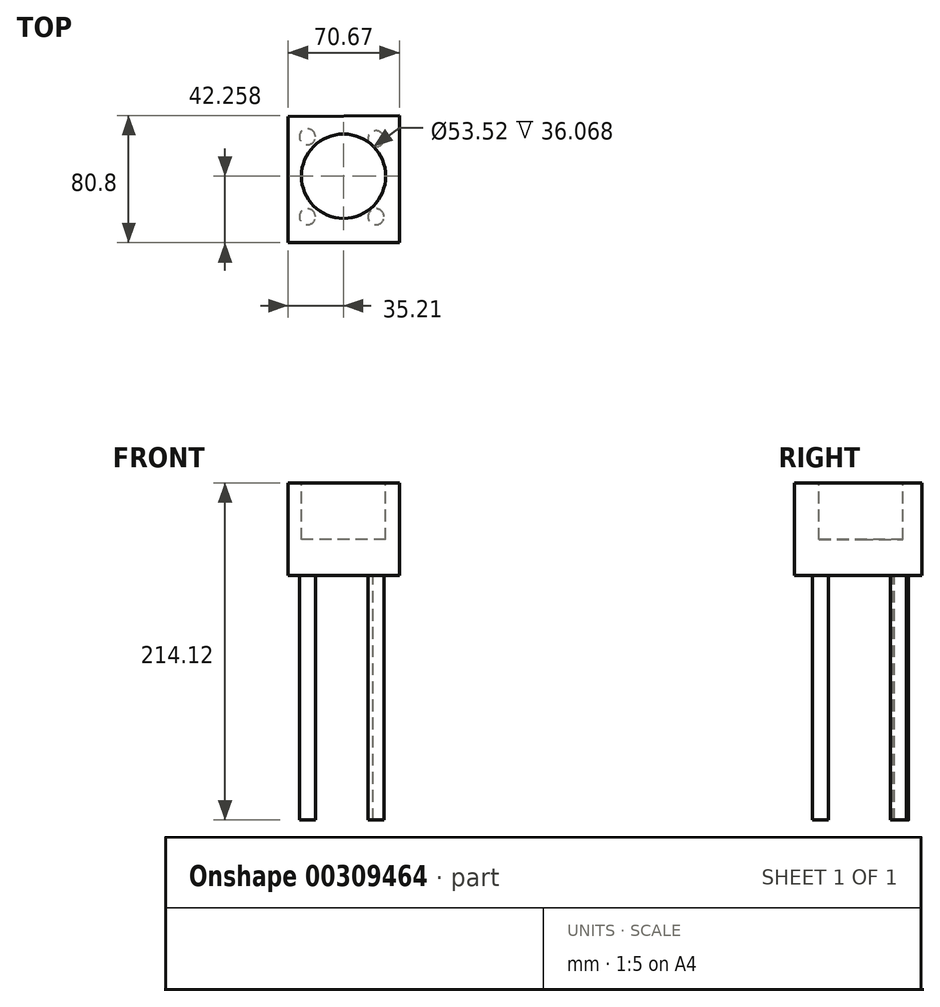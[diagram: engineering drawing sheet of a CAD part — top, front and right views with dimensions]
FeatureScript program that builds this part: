
annotation { "Feature Type Name" : "Feature", "Feature Type Description" : "" }
export const myFeature = defineFeature(function(context is Context, id is Id, definition is map)
    precondition{}
    {
        {
            var Q0;
            Q0=qCreatedBy(makeId("Top.planeOp"),FACE);
            var sketch = newSketch(context, id + "F0", { "sketchPlane" : qUnion([Q0])});
            skLineSegment(sketch, "E0", {"start": v(-35.21, 50.58) * mm, "end": v(-35.21, -29.63) * mm});
            skLineSegment(sketch, "E1", {"start": v(-35.21, -29.63) * mm, "end": v(35.46, -29.63) * mm});
            skLineSegment(sketch, "E2", {"start": v(35.46, -29.63) * mm, "end": v(35.46, 51.17) * mm});
            skLineSegment(sketch, "E3", {"start": v(35.46, 51.17) * mm, "end": v(-35.21, 50.58) * mm});
            skSolve(sketch);
        }
        {
            var Q0;
            Q0=makeQuery(id+"F0.imprint","IMPRINT",FACE,{"disambiguationData":[TD([[makeQuery(id+"F0.imprint","IMPRINT",EDGE,{"derivedFrom":sQuery(id+"F0.wireOp",EDGE,"E0")}),1.0]])]});
            extrude(context, id + "F1", {"entities" : qUnion([Q0]), "depth" : 58.67 * mm});
        }
        {
            var Q0;
            Q0=makeQuery(id+"F1.opExtrude","CAP_FACE",FACE,{"disambiguationData":[OSD([sQuery(id+"F0.wireOp",EDGE,"E0"),sQuery(id+"F0.wireOp",EDGE,"E1"),sQuery(id+"F0.wireOp",EDGE,"E2"),sQuery(id+"F0.wireOp",EDGE,"E3")])],"isStart":false});
            var sketch = newSketch(context, id + "F2", { "sketchPlane" : qUnion([Q0])});
            skCircle(sketch, "E4", {"center": v(0, 12.63) * mm, "radius": 26.76 * mm});
            skSolve(sketch);
        }
        {
            var Q0;
            Q0=makeQuery(id+"F2.imprint","IMPRINT",FACE,{"disambiguationData":[TD([[makeQuery(id+"F2.imprint","IMPRINT",EDGE,{"derivedFrom":sQuery(id+"F2.wireOp",EDGE,"E4")}),1.0]])]});
            extrude(context, id + "F3", {"entities" : qUnion([Q0]), "operationType" : NewBodyOperationType.REMOVE, "oppositeDirection" : true, "depth" : 36.07 * mm});
        }
        {
            var Q0;
            Q0=makeQuery(id+"F1.opExtrude","CAP_FACE",FACE,{"disambiguationData":[OSD([sQuery(id+"F0.wireOp",EDGE,"E0"),sQuery(id+"F0.wireOp",EDGE,"E1"),sQuery(id+"F0.wireOp",EDGE,"E2"),sQuery(id+"F0.wireOp",EDGE,"E3")])],"isStart":false});
            var sketch = newSketch(context, id + "F4", { "sketchPlane" : qUnion([Q0])});
            skCircle(sketch, "E5", {"center": v(-22.97, -13.11) * mm, "radius": 5.08 * mm});
            skCircle(sketch, "E6", {"center": v(20.6, -13.11) * mm, "radius": 5.08 * mm});
            skCircle(sketch, "E7", {"center": v(20.6, 36.42) * mm, "radius": 5.08 * mm});
            skCircle(sketch, "E8", {"center": v(-22.97, 37.69) * mm, "radius": 5.08 * mm});
            skSolve(sketch);
        }
        {
            var Q0;
            Q0=makeQuery(id+"F4.imprint","IMPRINT",FACE,{"disambiguationData":[TD([[makeQuery(id+"F4.imprint","IMPRINT",EDGE,{"derivedFrom":sQuery(id+"F4.wireOp",EDGE,"E5")}),1.0]])]});
            var Q1;
            Q1=makeQuery(id+"F4.imprint","IMPRINT",FACE,{"disambiguationData":[TD([[makeQuery(id+"F4.imprint","IMPRINT",EDGE,{"derivedFrom":sQuery(id+"F4.wireOp",EDGE,"E8")}),1.0]])]});
            var Q2;
            {var subQ0=sQuery(id+"F4.wireOp",EDGE,"E7");var subQ1=makeQuery(id+"F3.boolean.opBoolean","COPY",EDGE,{"derivedFrom":makeQuery(id+"F3.opExtrude","CAP_EDGE",EDGE,{"disambiguationData":[OSD([sQuery(id+"F2.wireOp",EDGE,"E4")])],"isStart":true})});var subQ2=makeQuery(id+"F4.imprint","INTERSECT",VERTEX,{"disambiguationData":[OD(0.0)],"derivedFrom":[subQ1,subQ0]});Q2=makeQuery(id+"F4.imprint","IMPRINT",FACE,{"disambiguationData":[TD([[makeQuery(id+"F4.imprint","IMPRINT",EDGE,{"disambiguationData":[TD([[subQ2,1.0]])],"derivedFrom":subQ0}),1.0]])]});}
            var Q3;
            Q3=makeQuery(id+"F4.imprint","IMPRINT",FACE,{"disambiguationData":[TD([[makeQuery(id+"F4.imprint","IMPRINT",EDGE,{"derivedFrom":sQuery(id+"F4.wireOp",EDGE,"E6")}),1.0]])]});
            extrude(context, id + "F5", {"entities" : qUnion([Q0, Q1, Q2, Q3]), "operationType" : NewBodyOperationType.ADD, "oppositeDirection" : true, "depth" : 214.12 * mm});
        }
    });
